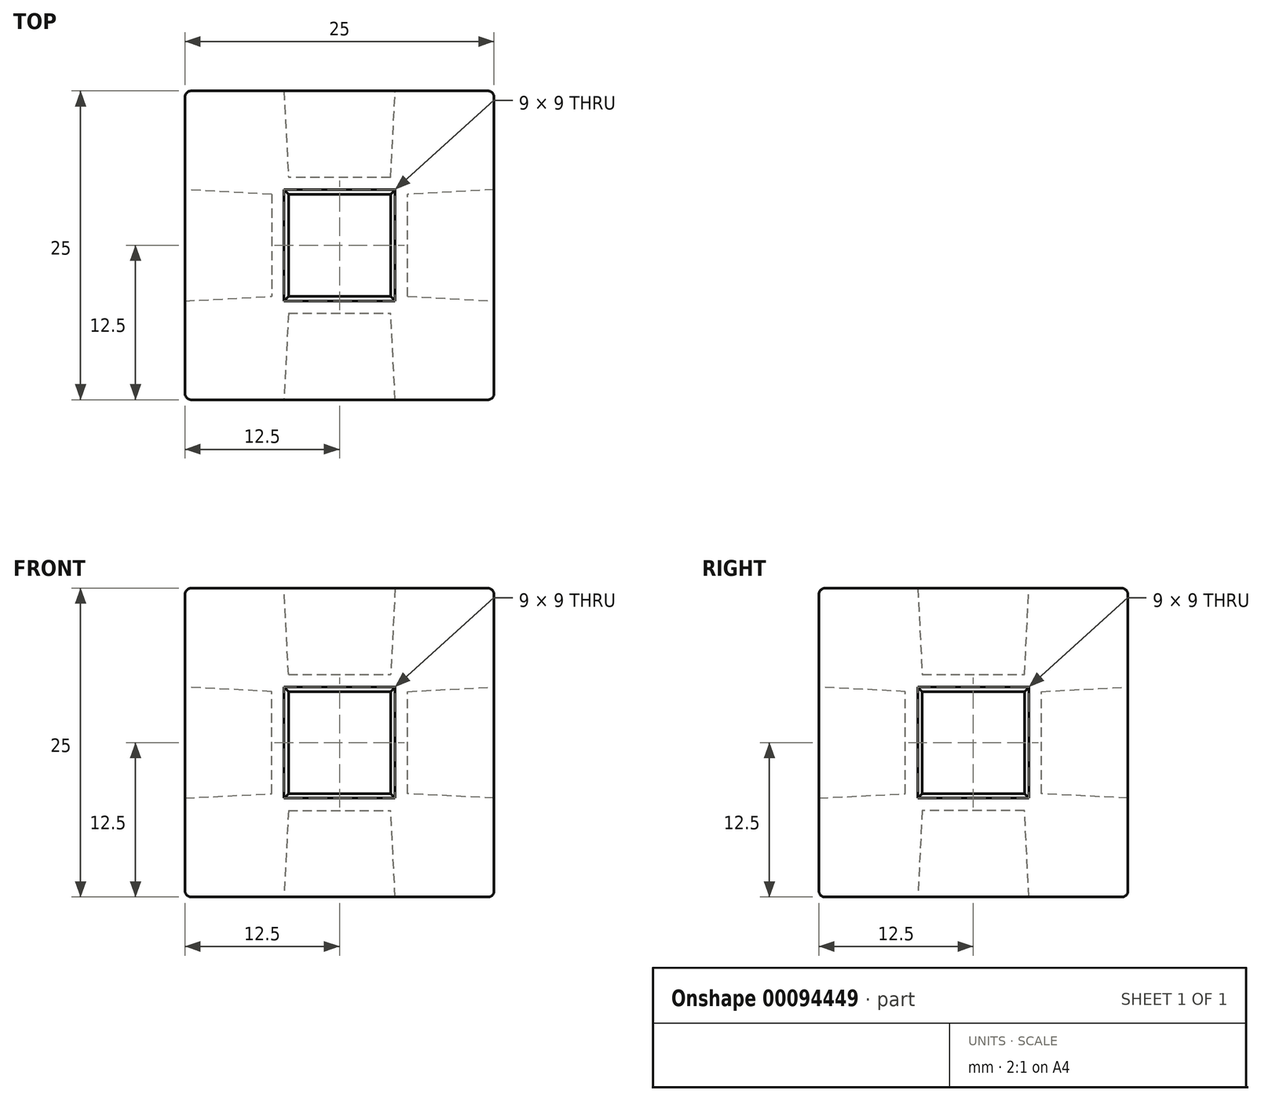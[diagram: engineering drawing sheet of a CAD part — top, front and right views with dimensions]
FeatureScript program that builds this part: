
annotation { "Feature Type Name" : "Feature", "Feature Type Description" : "" }
export const myFeature = defineFeature(function(context is Context, id is Id, definition is map)
    precondition{}
    {
        {
            var Q0;
            Q0=qCreatedBy(makeId("Top.planeOp"),FACE);
            var sketch = newSketch(context, id + "F0", { "sketchPlane" : qUnion([Q0])});
            skLineSegment(sketch, "E0.bottom", {"start": v(12.5, -12.5) * mm, "end": v(-12.5, -12.5) * mm});
            skLineSegment(sketch, "E0.top", {"start": v(12.5, 12.5) * mm, "end": v(-12.5, 12.5) * mm});
            skLineSegment(sketch, "E0.left", {"start": v(12.5, -12.5) * mm, "end": v(12.5, 12.5) * mm});
            skLineSegment(sketch, "E0.right", {"start": v(-12.5, -12.5) * mm, "end": v(-12.5, 12.5) * mm});
            skPoint(sketch, "E0.middle", {"position": v(0, 0) * mm});
            skSolve(sketch);
        }
        {
            var Q0;
            Q0=makeQuery(id+"F0.imprint","IMPRINT",FACE,{"disambiguationData":[TD([[makeQuery(id+"F0.imprint","IMPRINT",EDGE,{"derivedFrom":sQuery(id+"F0.wireOp",EDGE,"E0.bottom")}),-1.0]])]});
            extrude(context, id + "F1", {"entities" : qUnion([Q0]), "depth" : 25 * mm});
        }
        {
            var Q0;
            Q0=makeQuery(id+"F1.opExtrude","CAP_FACE",FACE,{"disambiguationData":[OSD([sQuery(id+"F0.wireOp",EDGE,"E0.bottom"),sQuery(id+"F0.wireOp",EDGE,"E0.top"),sQuery(id+"F0.wireOp",EDGE,"E0.left"),sQuery(id+"F0.wireOp",EDGE,"E0.right")])],"isStart":false});
            var sketch = newSketch(context, id + "F2", { "sketchPlane" : qUnion([Q0])});
            skLineSegment(sketch, "E1.bottom", {"start": v(4.5, -4.5) * mm, "end": v(-4.5, -4.5) * mm});
            skLineSegment(sketch, "E1.top", {"start": v(4.5, 4.5) * mm, "end": v(-4.5, 4.5) * mm});
            skLineSegment(sketch, "E1.left", {"start": v(4.5, -4.5) * mm, "end": v(4.5, 4.5) * mm});
            skLineSegment(sketch, "E1.right", {"start": v(-4.5, -4.5) * mm, "end": v(-4.5, 4.5) * mm});
            skPoint(sketch, "E1.middle", {"position": v(0, 0) * mm});
            skSolve(sketch);
        }
        {
            var Q0;
            Q0 = qSketchRegion(id + "F2", true);
            extrude(context, id + "F3", {"entities" : qUnion([Q0]), "operationType" : NewBodyOperationType.REMOVE, "oppositeDirection" : true, "depth" : 7 * mm, "hasDraft" : true, "draftAngle" : 3 * degree, "draftPullDirection" : true});
        }
        {
            var Q0;
            Q0=makeQuery(id+"F1.opExtrude","SWEPT_FACE",FACE,{"disambiguationData":[OSD([sQuery(id+"F0.wireOp",EDGE,"E0.bottom")])]});
            var sketch = newSketch(context, id + "F4", { "sketchPlane" : qUnion([Q0])});
            skLineSegment(sketch, "E2.bottom", {"start": v(4.5, 8) * mm, "end": v(-4.5, 8) * mm});
            skLineSegment(sketch, "E2.top", {"start": v(4.5, 17) * mm, "end": v(-4.5, 17) * mm});
            skLineSegment(sketch, "E2.left", {"start": v(4.5, 8) * mm, "end": v(4.5, 17) * mm});
            skLineSegment(sketch, "E2.right", {"start": v(-4.5, 8) * mm, "end": v(-4.5, 17) * mm});
            skPoint(sketch, "E2.middle", {"position": v(0, 12.5) * mm});
            skPoint(sketch, "E2.middle.positionSnap0", {"position": v(12.5, 12.5) * mm});
            skPoint(sketch, "E2.centerSnap0", {"position": v(12.5, 12.5) * mm});
            skSolve(sketch);
        }
        {
            var Q0;
            Q0=makeQuery(id+"F1.opExtrude","SWEPT_FACE",FACE,{"disambiguationData":[OSD([sQuery(id+"F0.wireOp",EDGE,"E0.top")])]});
            var sketch = newSketch(context, id + "F5", { "sketchPlane" : qUnion([Q0])});
            skLineSegment(sketch, "E3.bottom", {"start": v(4.5, 8) * mm, "end": v(-4.5, 8) * mm});
            skLineSegment(sketch, "E3.top", {"start": v(4.5, 17) * mm, "end": v(-4.5, 17) * mm});
            skLineSegment(sketch, "E3.left", {"start": v(4.5, 8) * mm, "end": v(4.5, 17) * mm});
            skLineSegment(sketch, "E3.right", {"start": v(-4.5, 8) * mm, "end": v(-4.5, 17) * mm});
            skPoint(sketch, "E3.middle", {"position": v(0, 12.5) * mm});
            skLineSegment(sketch, "E4", {"start": v(0, 0) * mm, "end": v(0, 25) * mm, "construction": true});
            skSolve(sketch);
        }
        {
            var Q0;
            Q0=makeQuery(id+"F1.opExtrude","SWEPT_FACE",FACE,{"disambiguationData":[OSD([sQuery(id+"F0.wireOp",EDGE,"E0.right")])]});
            var sketch = newSketch(context, id + "F6", { "sketchPlane" : qUnion([Q0])});
            skLineSegment(sketch, "E5.bottom", {"start": v(4.5, 8) * mm, "end": v(-4.5, 8) * mm});
            skLineSegment(sketch, "E5.top", {"start": v(4.5, 17) * mm, "end": v(-4.5, 17) * mm});
            skLineSegment(sketch, "E5.left", {"start": v(4.5, 8) * mm, "end": v(4.5, 17) * mm});
            skLineSegment(sketch, "E5.right", {"start": v(-4.5, 8) * mm, "end": v(-4.5, 17) * mm});
            skPoint(sketch, "E5.middle", {"position": v(0, 12.5) * mm});
            skLineSegment(sketch, "E6", {"start": v(0, 25) * mm, "end": v(0, 0) * mm, "construction": true});
            skSolve(sketch);
        }
        {
            var Q0;
            Q0=makeQuery(id+"F1.opExtrude","SWEPT_FACE",FACE,{"disambiguationData":[OSD([sQuery(id+"F0.wireOp",EDGE,"E0.left")])]});
            var sketch = newSketch(context, id + "F7", { "sketchPlane" : qUnion([Q0])});
            skLineSegment(sketch, "E7.bottom", {"start": v(4.5, 8) * mm, "end": v(-4.5, 8) * mm});
            skLineSegment(sketch, "E7.top", {"start": v(4.5, 17) * mm, "end": v(-4.5, 17) * mm});
            skLineSegment(sketch, "E7.left", {"start": v(4.5, 8) * mm, "end": v(4.5, 17) * mm});
            skLineSegment(sketch, "E7.right", {"start": v(-4.5, 8) * mm, "end": v(-4.5, 17) * mm});
            skPoint(sketch, "E7.middle", {"position": v(0, 12.5) * mm});
            skLineSegment(sketch, "E8", {"start": v(0, 25) * mm, "end": v(0, 0) * mm, "construction": true});
            skSolve(sketch);
        }
        {
            var Q0;
            Q0=makeQuery(id+"F1.opExtrude","CAP_FACE",FACE,{"disambiguationData":[OSD([sQuery(id+"F0.wireOp",EDGE,"E0.bottom"),sQuery(id+"F0.wireOp",EDGE,"E0.top"),sQuery(id+"F0.wireOp",EDGE,"E0.left"),sQuery(id+"F0.wireOp",EDGE,"E0.right")])],"isStart":true});
            var sketch = newSketch(context, id + "F8", { "sketchPlane" : qUnion([Q0])});
            skLineSegment(sketch, "E9.bottom", {"start": v(4.5, -4.5) * mm, "end": v(-4.5, -4.5) * mm});
            skLineSegment(sketch, "E9.top", {"start": v(4.5, 4.5) * mm, "end": v(-4.5, 4.5) * mm});
            skLineSegment(sketch, "E9.left", {"start": v(4.5, -4.5) * mm, "end": v(4.5, 4.5) * mm});
            skLineSegment(sketch, "E9.right", {"start": v(-4.5, -4.5) * mm, "end": v(-4.5, 4.5) * mm});
            skPoint(sketch, "E9.middle", {"position": v(0, 0) * mm});
            skSolve(sketch);
        }
        {
            var Q0;
            Q0 = qSketchRegion(id + "F4", true);
            extrude(context, id + "F9", {"entities" : qUnion([Q0]), "operationType" : NewBodyOperationType.REMOVE, "oppositeDirection" : true, "depth" : 7 * mm, "hasDraft" : true, "draftAngle" : 3 * degree, "draftPullDirection" : true});
        }
        {
            var Q0;
            Q0 = qSketchRegion(id + "F5", true);
            extrude(context, id + "F10", {"entities" : qUnion([Q0]), "operationType" : NewBodyOperationType.REMOVE, "oppositeDirection" : true, "depth" : 7 * mm, "hasDraft" : true, "draftAngle" : 3 * degree, "draftPullDirection" : true});
        }
        {
            var Q0;
            Q0 = qSketchRegion(id + "F6", true);
            extrude(context, id + "F11", {"entities" : qUnion([Q0]), "operationType" : NewBodyOperationType.REMOVE, "oppositeDirection" : true, "depth" : 7 * mm, "hasDraft" : true, "draftAngle" : 3 * degree, "draftPullDirection" : true});
        }
        {
            var Q0;
            Q0 = qSketchRegion(id + "F7", true);
            extrude(context, id + "F12", {"entities" : qUnion([Q0]), "operationType" : NewBodyOperationType.REMOVE, "oppositeDirection" : true, "depth" : 7 * mm, "hasDraft" : true, "draftAngle" : 3 * degree, "draftPullDirection" : true});
        }
        {
            var Q0;
            Q0 = qSketchRegion(id + "F8", true);
            extrude(context, id + "F13", {"entities" : qUnion([Q0]), "operationType" : NewBodyOperationType.REMOVE, "oppositeDirection" : true, "depth" : 7 * mm, "hasDraft" : true, "draftAngle" : 3 * degree, "draftPullDirection" : true});
        }
        {
            var Q0;
            Q0=makeQuery(id+"F3.boolean.opBoolean","COPY",EDGE,{"derivedFrom":makeQuery(id+"F3.opExtrude","CAP_EDGE",EDGE,{"disambiguationData":[OSD([sQuery(id+"F2.wireOp",EDGE,"E1.right")])],"isStart":true})});
            var Q1;
            Q1=makeQuery(id+"F3.boolean.opBoolean","COPY",EDGE,{"derivedFrom":makeQuery(id+"F3.opExtrude","CAP_EDGE",EDGE,{"disambiguationData":[OSD([sQuery(id+"F2.wireOp",EDGE,"E1.top")])],"isStart":true})});
            var Q2;
            Q2=makeQuery(id+"F3.boolean.opBoolean","COPY",EDGE,{"derivedFrom":makeQuery(id+"F3.opExtrude","CAP_EDGE",EDGE,{"disambiguationData":[OSD([sQuery(id+"F2.wireOp",EDGE,"E1.bottom")])],"isStart":true})});
            var Q3;
            Q3=makeQuery(id+"F3.boolean.opBoolean","COPY",EDGE,{"derivedFrom":makeQuery(id+"F3.opExtrude","CAP_EDGE",EDGE,{"disambiguationData":[OSD([sQuery(id+"F2.wireOp",EDGE,"E1.left")])],"isStart":true})});
            var Q4;
            Q4=makeQuery(id+"F13.boolean.opBoolean","COPY",EDGE,{"derivedFrom":makeQuery(id+"F13.opExtrude","CAP_EDGE",EDGE,{"disambiguationData":[OSD([sQuery(id+"F8.wireOp",EDGE,"E9.right")])],"isStart":true})});
            var Q5;
            Q5=makeQuery(id+"F13.boolean.opBoolean","COPY",EDGE,{"derivedFrom":makeQuery(id+"F13.opExtrude","CAP_EDGE",EDGE,{"disambiguationData":[OSD([sQuery(id+"F8.wireOp",EDGE,"E9.bottom")])],"isStart":true})});
            var Q6;
            Q6=makeQuery(id+"F13.boolean.opBoolean","COPY",EDGE,{"derivedFrom":makeQuery(id+"F13.opExtrude","CAP_EDGE",EDGE,{"disambiguationData":[OSD([sQuery(id+"F8.wireOp",EDGE,"E9.left")])],"isStart":true})});
            var Q7;
            Q7=makeQuery(id+"F13.boolean.opBoolean","COPY",EDGE,{"derivedFrom":makeQuery(id+"F13.opExtrude","CAP_EDGE",EDGE,{"disambiguationData":[OSD([sQuery(id+"F8.wireOp",EDGE,"E9.top")])],"isStart":true})});
            var Q8;
            Q8=makeQuery(id+"F12.boolean.opBoolean","COPY",EDGE,{"derivedFrom":makeQuery(id+"F12.opExtrude","CAP_EDGE",EDGE,{"disambiguationData":[OSD([sQuery(id+"F7.wireOp",EDGE,"E7.bottom")])],"isStart":true})});
            var Q9;
            Q9=makeQuery(id+"F12.boolean.opBoolean","COPY",EDGE,{"derivedFrom":makeQuery(id+"F12.opExtrude","CAP_EDGE",EDGE,{"disambiguationData":[OSD([sQuery(id+"F7.wireOp",EDGE,"E7.right")])],"isStart":true})});
            var Q10;
            Q10=makeQuery(id+"F12.boolean.opBoolean","COPY",EDGE,{"derivedFrom":makeQuery(id+"F12.opExtrude","CAP_EDGE",EDGE,{"disambiguationData":[OSD([sQuery(id+"F7.wireOp",EDGE,"E7.top")])],"isStart":true})});
            var Q11;
            Q11=makeQuery(id+"F12.boolean.opBoolean","COPY",EDGE,{"derivedFrom":makeQuery(id+"F12.opExtrude","CAP_EDGE",EDGE,{"disambiguationData":[OSD([sQuery(id+"F7.wireOp",EDGE,"E7.left")])],"isStart":true})});
            var Q12;
            Q12=makeQuery(id+"F10.boolean.opBoolean","COPY",EDGE,{"derivedFrom":makeQuery(id+"F10.opExtrude","CAP_EDGE",EDGE,{"disambiguationData":[OSD([sQuery(id+"F5.wireOp",EDGE,"E3.top")])],"isStart":true})});
            var Q13;
            Q13=makeQuery(id+"F10.boolean.opBoolean","COPY",EDGE,{"derivedFrom":makeQuery(id+"F10.opExtrude","CAP_EDGE",EDGE,{"disambiguationData":[OSD([sQuery(id+"F5.wireOp",EDGE,"E3.left")])],"isStart":true})});
            var Q14;
            Q14=makeQuery(id+"F10.boolean.opBoolean","COPY",EDGE,{"derivedFrom":makeQuery(id+"F10.opExtrude","CAP_EDGE",EDGE,{"disambiguationData":[OSD([sQuery(id+"F5.wireOp",EDGE,"E3.bottom")])],"isStart":true})});
            var Q15;
            Q15=makeQuery(id+"F10.boolean.opBoolean","COPY",EDGE,{"derivedFrom":makeQuery(id+"F10.opExtrude","CAP_EDGE",EDGE,{"disambiguationData":[OSD([sQuery(id+"F5.wireOp",EDGE,"E3.right")])],"isStart":true})});
            var Q16;
            Q16=makeQuery(id+"F9.boolean.opBoolean","COPY",EDGE,{"derivedFrom":makeQuery(id+"F9.opExtrude","CAP_EDGE",EDGE,{"disambiguationData":[OSD([sQuery(id+"F4.wireOp",EDGE,"E2.bottom")])],"isStart":true})});
            var Q17;
            Q17=makeQuery(id+"F9.boolean.opBoolean","COPY",EDGE,{"derivedFrom":makeQuery(id+"F9.opExtrude","CAP_EDGE",EDGE,{"disambiguationData":[OSD([sQuery(id+"F4.wireOp",EDGE,"E2.right")])],"isStart":true})});
            var Q18;
            Q18=makeQuery(id+"F9.boolean.opBoolean","COPY",EDGE,{"derivedFrom":makeQuery(id+"F9.opExtrude","CAP_EDGE",EDGE,{"disambiguationData":[OSD([sQuery(id+"F4.wireOp",EDGE,"E2.top")])],"isStart":true})});
            var Q19;
            Q19=makeQuery(id+"F9.boolean.opBoolean","COPY",EDGE,{"derivedFrom":makeQuery(id+"F9.opExtrude","CAP_EDGE",EDGE,{"disambiguationData":[OSD([sQuery(id+"F4.wireOp",EDGE,"E2.left")])],"isStart":true})});
            var Q20;
            Q20=makeQuery(id+"F11.boolean.opBoolean","COPY",EDGE,{"derivedFrom":makeQuery(id+"F11.opExtrude","CAP_EDGE",EDGE,{"disambiguationData":[OSD([sQuery(id+"F6.wireOp",EDGE,"E5.right")])],"isStart":true})});
            var Q21;
            Q21=makeQuery(id+"F11.boolean.opBoolean","COPY",EDGE,{"derivedFrom":makeQuery(id+"F11.opExtrude","CAP_EDGE",EDGE,{"disambiguationData":[OSD([sQuery(id+"F6.wireOp",EDGE,"E5.top")])],"isStart":true})});
            var Q22;
            Q22=makeQuery(id+"F11.boolean.opBoolean","COPY",EDGE,{"derivedFrom":makeQuery(id+"F11.opExtrude","CAP_EDGE",EDGE,{"disambiguationData":[OSD([sQuery(id+"F6.wireOp",EDGE,"E5.left")])],"isStart":true})});
            var Q23;
            Q23=makeQuery(id+"F11.boolean.opBoolean","COPY",EDGE,{"derivedFrom":makeQuery(id+"F11.opExtrude","CAP_EDGE",EDGE,{"disambiguationData":[OSD([sQuery(id+"F6.wireOp",EDGE,"E5.bottom")])],"isStart":true})});
            var Q24;
            Q24=makeQuery(id+"F1.opExtrude","SWEPT_EDGE",EDGE,{"disambiguationData":[OSD([sQuery(id+"F0.wireOp",EDGE,"E0.bottom"),sQuery(id+"F0.wireOp",EDGE,"E0.right")])]});
            var Q25;
            Q25=makeQuery(id+"F1.opExtrude","CAP_EDGE",EDGE,{"disambiguationData":[OSD([sQuery(id+"F0.wireOp",EDGE,"E0.right")])],"isStart":true});
            var Q26;
            Q26=makeQuery(id+"F1.opExtrude","CAP_EDGE",EDGE,{"disambiguationData":[OSD([sQuery(id+"F0.wireOp",EDGE,"E0.right")])],"isStart":false});
            var Q27;
            Q27=makeQuery(id+"F1.opExtrude","SWEPT_EDGE",EDGE,{"disambiguationData":[OSD([sQuery(id+"F0.wireOp",EDGE,"E0.top"),sQuery(id+"F0.wireOp",EDGE,"E0.right")])]});
            var Q28;
            Q28=makeQuery(id+"F1.opExtrude","CAP_EDGE",EDGE,{"disambiguationData":[OSD([sQuery(id+"F0.wireOp",EDGE,"E0.top")])],"isStart":false});
            var Q29;
            Q29=makeQuery(id+"F1.opExtrude","CAP_EDGE",EDGE,{"disambiguationData":[OSD([sQuery(id+"F0.wireOp",EDGE,"E0.left")])],"isStart":false});
            var Q30;
            Q30=makeQuery(id+"F1.opExtrude","CAP_EDGE",EDGE,{"disambiguationData":[OSD([sQuery(id+"F0.wireOp",EDGE,"E0.bottom")])],"isStart":false});
            var Q31;
            Q31=makeQuery(id+"F1.opExtrude","SWEPT_EDGE",EDGE,{"disambiguationData":[OSD([sQuery(id+"F0.wireOp",EDGE,"E0.bottom"),sQuery(id+"F0.wireOp",EDGE,"E0.left")])]});
            var Q32;
            Q32=makeQuery(id+"F1.opExtrude","CAP_EDGE",EDGE,{"disambiguationData":[OSD([sQuery(id+"F0.wireOp",EDGE,"E0.bottom")])],"isStart":true});
            var Q33;
            Q33=makeQuery(id+"F1.opExtrude","CAP_EDGE",EDGE,{"disambiguationData":[OSD([sQuery(id+"F0.wireOp",EDGE,"E0.left")])],"isStart":true});
            var Q34;
            Q34=makeQuery(id+"F1.opExtrude","SWEPT_EDGE",EDGE,{"disambiguationData":[OSD([sQuery(id+"F0.wireOp",EDGE,"E0.top"),sQuery(id+"F0.wireOp",EDGE,"E0.left")])]});
            var Q35;
            Q35=makeQuery(id+"F1.opExtrude","CAP_EDGE",EDGE,{"disambiguationData":[OSD([sQuery(id+"F0.wireOp",EDGE,"E0.top")])],"isStart":true});
            fillet(context, id + "F14", {"entities" : qUnion([Q0, Q1, Q2, Q3, Q4, Q5, Q6, Q7, Q8, Q9, Q10, Q11, Q12, Q13, Q14, Q15, Q16, Q17, Q18, Q19, Q20, Q21, Q22, Q23, Q24, Q25, Q26, Q27, Q28, Q29, Q30, Q31, Q32, Q33, Q34, Q35]), "radius" : 0.5 * mm, "tangentPropagation" : true, "allowEdgeOverflow" : false});
        }
    });
